# Revit family: 93806122
name_source: partatom
category: Modelos genéricos
revit_build: Autodesk Revit 2016 (Build: 20150220_1215(x64)
units: mm (PartAtom-declared; Revit-internal decimal feet)

## family parameters
Com base no plano de trabalho = Não
Compartilhado = Não
Corte com vazios quando carregados = Não
Cota do conector redondo = Utilizar diâmetro
Pode hospedar o vergalhão = Não
Ponto de cálculo do ambiente = Não
Sempre na vertical = Sim
Tipo de parte = Normal

## types (1)
- Tramontina - Morgana 93806122
    Código de montagem = 93806122
    Descrição = Tramontina Morgana 93806122
    Desenvolvedor = Factory Cursos
    Diametro do cano de saida = 34
    Fabricante = Tramontina
    Furação para torneira e misturador de sabão = DIA 35 mm
    Manual de Instalação = <Nenhum>
    Material = Aço inox AISI 304
    Modelo = Tramontina Morgana
    Nicho de instalação = 670 X 470 mm
    Site do desenvolvedor = www.factorycursos.com.br
    Tamanho (mm) = 685 X 485 X 203 (Profundidade)
    Tipo de imagem = <Nenhum>
    URL = http://www.tramontina.com.br
